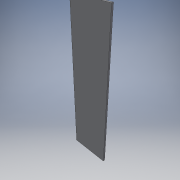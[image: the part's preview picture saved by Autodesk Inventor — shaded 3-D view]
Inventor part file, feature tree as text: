
AUTODESK INVENTOR PART (.ipt)
format: ipt  version: 2016 (Build 200138000, 138)  size: 89,088 bytes
history: native  units: in
note: dims shown in document units (in); Inventor stores cm internally (conversion verified against a paired STEP export)
features: extrude x1, sketch x1
ambient origin geometry x8: Origin, YZ Plane, XZ Plane, XY Plane, X Axis, Y Axis, Z Axis, Center Point
bodies: Solid1 (feature_tree)
feature tree (2):
  extrude  "Extrusion1"  Depth=16.0in
  sketch  "Sketch1"  dims[d0=62.0in d1=16.0in d2=0.75in d3=0.0in]
